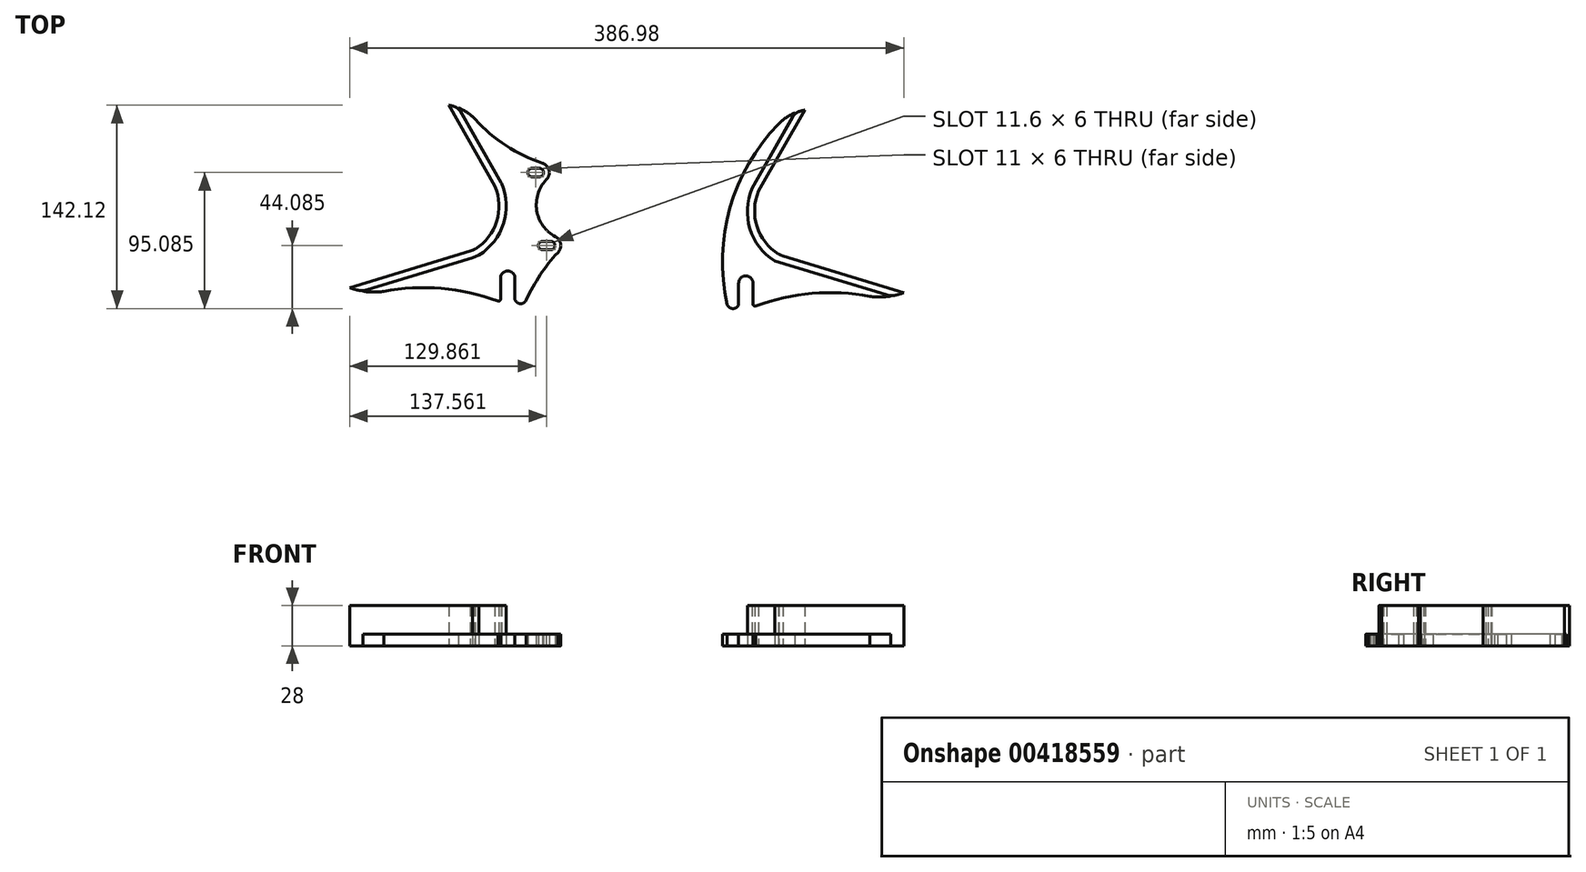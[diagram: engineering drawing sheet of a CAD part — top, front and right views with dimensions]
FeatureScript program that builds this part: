
annotation { "Feature Type Name" : "Feature", "Feature Type Description" : "" }
export const myFeature = defineFeature(function(context is Context, id is Id, definition is map)
    precondition{}
    {
        {
            var Q0;
            Q0=qCreatedBy(makeId("Top.planeOp"),FACE);
            var sketch = newSketch(context, id + "F0", { "sketchPlane" : qUnion([Q0])});
            skArc(sketch, "E0", {"start": v(92.06, 11.01) * mm, "mid": v(90.9, -13.55) * mm, "end": v(105.95, -33) * mm});
            skLineSegment(sketch, "E1", {"start": v(105.95, -33) * mm, "end": v(106.16, -33.11) * mm});
            skLineSegment(sketch, "E2", {"start": v(106.16, -33.11) * mm, "end": v(107.42, -33.6) * mm});
            skLineSegment(sketch, "E3", {"start": v(107.42, -33.6) * mm, "end": v(109.2, -34.29) * mm});
            skLineSegment(sketch, "E4", {"start": v(109.2, -34.29) * mm, "end": v(193.49, -59.91) * mm});
            skArc(sketch, "E5", {"start": v(88.13, -53.19) * mm, "mid": v(83.13, -48.19) * mm, "end": v(78.13, -53.19) * mm});
            skArc(sketch, "E6", {"start": v(88.13, -68.19) * mm, "mid": v(88.92, -69.1) * mm, "end": v(90.13, -69.19) * mm});
            skLineSegment(sketch, "E7", {"start": v(88.13, -53.19) * mm, "end": v(88.13, -68.19) * mm});
            skLineSegment(sketch, "E8", {"start": v(78.13, -53.19) * mm, "end": v(78.13, -68.19) * mm});
            skArc(sketch, "E9", {"start": v(70.13, -68.19) * mm, "mid": v(74.13, -71.06) * mm, "end": v(78.13, -68.19) * mm});
            skArc(sketch, "E10", {"start": v(169.82, -62.54) * mm, "mid": v(129.52, -60.4) * mm, "end": v(90.13, -69.19) * mm});
            skLineSegment(sketch, "E11", {"start": v(124.34, 67.6) * mm, "end": v(92.06, 11.01) * mm});
            skArc(sketch, "E12", {"start": v(105.82, 57.7) * mm, "mid": v(72.04, -0.73) * mm, "end": v(70.13, -68.19) * mm});
            skArc(sketch, "E13", {"start": v(-105.95, -29.54) * mm, "mid": v(-90.9, -10.09) * mm, "end": v(-92.06, 14.47) * mm});
            skLineSegment(sketch, "E14", {"start": v(-105.95, -29.54) * mm, "end": v(-106.16, -29.65) * mm});
            skLineSegment(sketch, "E15", {"start": v(-106.16, -29.65) * mm, "end": v(-107.42, -30.14) * mm});
            skLineSegment(sketch, "E16", {"start": v(-107.42, -30.14) * mm, "end": v(-109.2, -30.83) * mm});
            skLineSegment(sketch, "E17", {"start": v(-109.2, -30.83) * mm, "end": v(-193.49, -56.45) * mm});
            skArc(sketch, "E18", {"start": v(-103.3, -33.77) * mm, "mid": v(-86.14, -11.6) * mm, "end": v(-87.46, 16.42) * mm});
            skLineSegment(sketch, "E19", {"start": v(-107.75, -35.61) * mm, "end": v(-103.3, -33.77) * mm});
            skLineSegment(sketch, "E20", {"start": v(-87.72, 16.95) * mm, "end": v(-87.46, 16.42) * mm});
            skArc(sketch, "E21", {"start": v(-78.13, -49.73) * mm, "mid": v(-83.13, -44.73) * mm, "end": v(-88.13, -49.73) * mm});
            skArc(sketch, "E22", {"start": v(-90.13, -65.73) * mm, "mid": v(-88.92, -65.64) * mm, "end": v(-88.13, -64.73) * mm});
            skLineSegment(sketch, "E23", {"start": v(-88.13, -49.73) * mm, "end": v(-88.13, -64.73) * mm});
            skLineSegment(sketch, "E24", {"start": v(-78.13, -49.73) * mm, "end": v(-78.13, -64.73) * mm});
            skArc(sketch, "E25", {"start": v(-53.13, -29.98) * mm, "mid": v(-50.13, -26.98) * mm, "end": v(-53.13, -23.98) * mm});
            skArc(sketch, "E26", {"start": v(-61.13, 21.02) * mm, "mid": v(-58.13, 24.02) * mm, "end": v(-61.13, 27.02) * mm});
            skArc(sketch, "E27", {"start": v(-105.82, 61.16) * mm, "mid": v(-84.33, 42.8) * mm, "end": v(-58.82, 30.63) * mm});
            skArc(sketch, "E28", {"start": v(-58.73, -23.98) * mm, "mid": v(-60.85, -24.85) * mm, "end": v(-61.73, -26.98) * mm});
            skArc(sketch, "E29", {"start": v(-61.73, -26.98) * mm, "mid": v(-60.85, -29.1) * mm, "end": v(-58.73, -29.98) * mm});
            skLineSegment(sketch, "E30", {"start": v(-58.73, -29.98) * mm, "end": v(-53.13, -29.98) * mm});
            skLineSegment(sketch, "E31", {"start": v(-58.73, -23.98) * mm, "end": v(-53.13, -23.98) * mm});
            skArc(sketch, "E32", {"start": v(-66.13, 27.02) * mm, "mid": v(-68.25, 26.15) * mm, "end": v(-69.13, 24.02) * mm});
            skArc(sketch, "E33", {"start": v(-69.13, 24.02) * mm, "mid": v(-68.25, 21.9) * mm, "end": v(-66.13, 21.02) * mm});
            skLineSegment(sketch, "E34", {"start": v(-66.13, 21.02) * mm, "end": v(-61.13, 21.02) * mm});
            skLineSegment(sketch, "E35", {"start": v(-66.13, 27.02) * mm, "end": v(-61.13, 27.02) * mm});
            skArc(sketch, "E36", {"start": v(-56.34, 18.92) * mm, "mid": v(-62.84, -2.56) * mm, "end": v(-49.8, -20.82) * mm});
            skArc(sketch, "E37", {"start": v(-56.34, 18.92) * mm, "mid": v(-54.31, 25.62) * mm, "end": v(-59.1, 30.72) * mm});
            skArc(sketch, "E38", {"start": v(-48.17, -31.92) * mm, "mid": v(-46.2, -25.95) * mm, "end": v(-49.82, -20.8) * mm});
            skArc(sketch, "E39", {"start": v(-48.17, -31.92) * mm, "mid": v(-60.46, -47.44) * mm, "end": v(-70.13, -64.73) * mm});
            skArc(sketch, "E40", {"start": v(-78.13, -64.73) * mm, "mid": v(-74.13, -67.6) * mm, "end": v(-70.13, -64.73) * mm});
            skArc(sketch, "E41", {"start": v(-90.13, -65.73) * mm, "mid": v(-129.52, -56.93) * mm, "end": v(-169.82, -59.08) * mm});
            skLineSegment(sketch, "E42", {"start": v(-107.75, -35.61) * mm, "end": v(-184.27, -58.87) * mm});
            skLineSegment(sketch, "E43", {"start": v(-117.5, 69.16) * mm, "end": v(-87.72, 16.95) * mm});
            skLineSegment(sketch, "E44", {"start": v(-124.34, 71.06) * mm, "end": v(-92.06, 14.47) * mm});
            skArc(sketch, "E45", {"start": v(-105.82, 61.16) * mm, "mid": v(-111.22, 65.8) * mm, "end": v(-117.5, 69.16) * mm});
            skArc(sketch, "E46", {"start": v(-117.5, 69.16) * mm, "mid": v(-120.87, 70.3) * mm, "end": v(-124.34, 71.06) * mm});
            skArc(sketch, "E47", {"start": v(-193.49, -56.45) * mm, "mid": v(-188.94, -57.88) * mm, "end": v(-184.27, -58.87) * mm});
            skArc(sketch, "E48", {"start": v(-184.27, -58.87) * mm, "mid": v(-177.05, -59.5) * mm, "end": v(-169.82, -59.08) * mm});
            skArc(sketch, "E49", {"start": v(169.82, -62.54) * mm, "mid": v(177.05, -62.97) * mm, "end": v(184.27, -62.34) * mm});
            skArc(sketch, "E50", {"start": v(184.27, -62.34) * mm, "mid": v(188.94, -61.35) * mm, "end": v(193.49, -59.91) * mm});
            skArc(sketch, "E51", {"start": v(124.34, 67.6) * mm, "mid": v(120.87, 66.84) * mm, "end": v(117.5, 65.7) * mm});
            skArc(sketch, "E52", {"start": v(117.5, 65.7) * mm, "mid": v(111.22, 62.34) * mm, "end": v(105.82, 57.7) * mm});
            skLineSegment(sketch, "E53", {"start": v(117.5, 65.7) * mm, "end": v(87.46, 12.96) * mm});
            skArc(sketch, "E54", {"start": v(87.46, 12.96) * mm, "mid": v(86.03, -15.31) * mm, "end": v(103.27, -37.76) * mm});
            skLineSegment(sketch, "E55", {"start": v(103.27, -37.76) * mm, "end": v(184.27, -62.34) * mm});
            skSolve(sketch);
        }
        {
            var Q0;
            Q0=makeQuery(id+"F0.imprint","IMPRINT",FACE,{"disambiguationData":[TD([[makeQuery(id+"F0.imprint","IMPRINT",EDGE,{"derivedFrom":sQuery(id+"F0.wireOp",EDGE,"E18")}),-1.0]])]});
            var Q1;
            Q1=makeQuery(id+"F0.imprint","IMPRINT",FACE,{"disambiguationData":[TD([[makeQuery(id+"F0.imprint","IMPRINT",EDGE,{"derivedFrom":sQuery(id+"F0.wireOp",EDGE,"E5")}),-1.0]])]});
            extrude(context, id + "F1", {"entities" : qUnion([Q0, Q1]), "depth" : 8 * mm});
        }
        {
            var Q0;
            Q0=makeQuery(id+"F0.imprint","IMPRINT",FACE,{"disambiguationData":[TD([[makeQuery(id+"F0.imprint","IMPRINT",EDGE,{"derivedFrom":sQuery(id+"F0.wireOp",EDGE,"E13")}),-1.0]])]});
            var Q1;
            Q1=makeQuery(id+"F0.imprint","IMPRINT",FACE,{"disambiguationData":[TD([[makeQuery(id+"F0.imprint","IMPRINT",EDGE,{"derivedFrom":sQuery(id+"F0.wireOp",EDGE,"E0")}),-1.0]])]});
            extrude(context, id + "F2", {"entities" : qUnion([Q0, Q1]), "depth" : 28 * mm});
        }
        {
            var Q0;
            Q0=makeQuery(id+"F2.opExtrude","SWEPT_EDGE",EDGE,{"disambiguationData":[OSD([sQuery(id+"F0.wireOp",EDGE,"E42"),sQuery(id+"F0.wireOp",EDGE,"E47"),sQuery(id+"F0.wireOp",EDGE,"E48")])]});
            var Q1;
            Q1=makeQuery(id+"F2.opExtrude","SWEPT_EDGE",EDGE,{"disambiguationData":[OSD([sQuery(id+"F0.wireOp",EDGE,"E49"),sQuery(id+"F0.wireOp",EDGE,"E50"),sQuery(id+"F0.wireOp",EDGE,"E55")])]});
            fillet(context, id + "F3", {"entities" : qUnion([Q0, Q1]), "radius" : 13 * mm, "tangentPropagation" : true, "allowEdgeOverflow" : false});
        }
        {
            var Q0;
            Q0=makeQuery(id+"F2.opExtrude","SWEPT_EDGE",EDGE,{"disambiguationData":[OSD([sQuery(id+"F0.wireOp",EDGE,"E43"),sQuery(id+"F0.wireOp",EDGE,"E45"),sQuery(id+"F0.wireOp",EDGE,"E46")])]});
            var Q1;
            Q1=makeQuery(id+"F2.opExtrude","SWEPT_EDGE",EDGE,{"disambiguationData":[OSD([sQuery(id+"F0.wireOp",EDGE,"E51"),sQuery(id+"F0.wireOp",EDGE,"E52"),sQuery(id+"F0.wireOp",EDGE,"E53")])]});
            fillet(context, id + "F4", {"entities" : qUnion([Q0, Q1]), "radius" : 9 * mm, "tangentPropagation" : true, "allowEdgeOverflow" : false});
        }
    });
